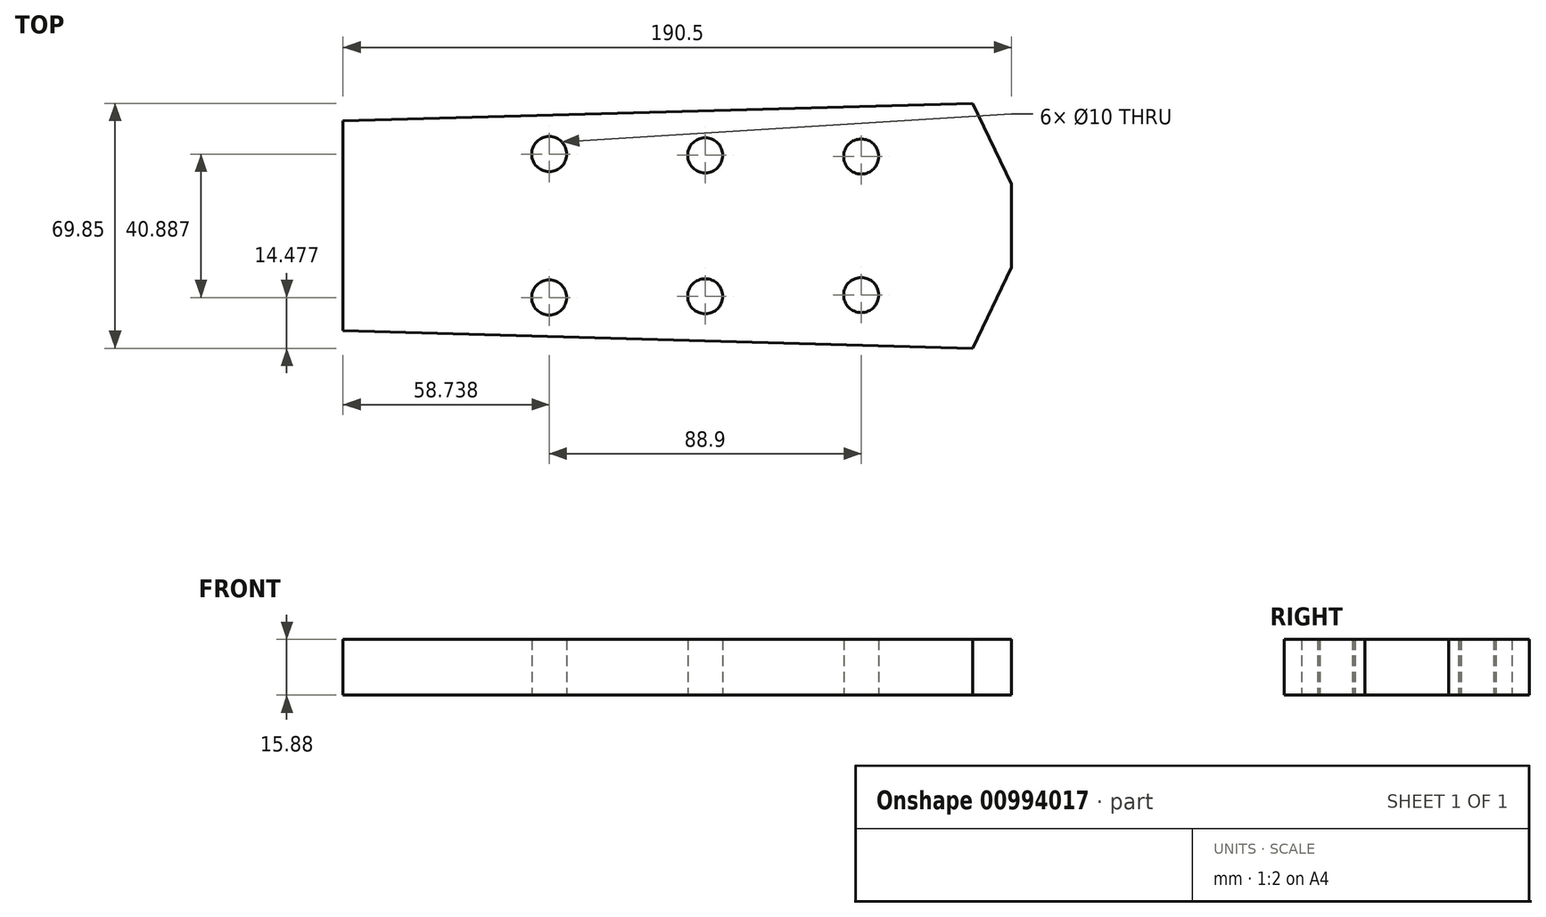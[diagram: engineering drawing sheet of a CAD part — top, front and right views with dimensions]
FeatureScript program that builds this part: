
annotation { "Feature Type Name" : "Feature", "Feature Type Description" : "" }
export const myFeature = defineFeature(function(context is Context, id is Id, definition is map)
    precondition{}
    {
        {
            var Q0;
            Q0=qCreatedBy(makeId("Top.planeOp"),FACE);
            var sketch = newSketch(context, id + "F0", { "sketchPlane" : qUnion([Q0])});
            skLineSegment(sketch, "E0", {"start": v(0, 0) * mm, "end": v(-179.39, 0) * mm, "construction": true});
            skLineSegment(sketch, "E1", {"start": v(0, 0) * mm, "end": v(0, 11.9) * mm});
            skLineSegment(sketch, "E2.bottom", {"start": v(-179.39, 0) * mm, "end": v(-11.11, 0) * mm, "construction": true});
            skLineSegment(sketch, "E2.left", {"start": v(-179.39, 0) * mm, "end": v(-179.39, 30.23) * mm, "construction": true});
            skPoint(sketch, "E3", {"position": v(-179.39, 30.23) * mm});
            skLineSegment(sketch, "E4", {"start": v(-11.11, 34.92) * mm, "end": v(0, 11.9) * mm});
            skLineSegment(sketch, "E5", {"start": v(-131.76, 31.56) * mm, "end": v(-131.76, 20.44) * mm, "construction": true});
            skLineSegment(sketch, "E6", {"start": v(-87.31, 20.1) * mm, "end": v(-87.31, 32.8) * mm, "construction": true});
            skLineSegment(sketch, "E7", {"start": v(-42.86, 19.75) * mm, "end": v(-42.86, 34.04) * mm, "construction": true});
            skCircle(sketch, "E8", {"center": v(-131.76, 20.44) * mm, "radius": 5 * mm});
            skCircle(sketch, "E9", {"center": v(-87.31, 20.1) * mm, "radius": 5 * mm});
            skCircle(sketch, "E10", {"center": v(-42.86, 19.75) * mm, "radius": 5 * mm});
            skLineSegment(sketch, "E11", {"start": v(-190.5, 29.92) * mm, "end": v(-190.5, 0) * mm});
            skLineSegment(sketch, "E12", {"start": v(-11.11, 0) * mm, "end": v(-11.11, 34.93) * mm, "construction": true});
            skLineSegment(sketch, "E13", {"start": v(-11.11, 34.92) * mm, "end": v(-190.5, 29.92) * mm});
            skLineSegment(sketch, "E14", {"start": v(-179.39, 0) * mm, "end": v(-190.5, 0) * mm, "construction": true});
            skLineSegment(sketch, "E15.MirrorCS", {"start": v(-190.5, -29.92) * mm, "end": v(-190.5, 0) * mm});
            skLineSegment(sketch, "E16.MirrorCS", {"start": v(-11.11, -34.93) * mm, "end": v(-190.5, -29.92) * mm});
            skLineSegment(sketch, "E17.MirrorCS", {"start": v(-11.11, -34.93) * mm, "end": v(0, -11.9) * mm});
            skLineSegment(sketch, "E18.MirrorCS", {"start": v(0, 0) * mm, "end": v(0, -11.9) * mm});
            skCircle(sketch, "E19.MirrorC", {"center": v(-42.86, -19.75) * mm, "radius": 5 * mm});
            skCircle(sketch, "E20.MirrorC", {"center": v(-87.31, -20.1) * mm, "radius": 5 * mm});
            skCircle(sketch, "E21.MirrorC", {"center": v(-131.76, -20.44) * mm, "radius": 5 * mm});
            skPoint(sketch, "E22", {"position": v(-179.39, -30.23) * mm});
            skSolve(sketch);
        }
        {
            var Q0;
            Q0=makeQuery(id+"F0.imprint","IMPRINT",FACE,{"disambiguationData":[TD([[makeQuery(id+"F0.imprint","IMPRINT",EDGE,{"derivedFrom":sQuery(id+"F0.wireOp",EDGE,"E1")}),1.0]])]});
            extrude(context, id + "F1", {"entities" : qUnion([Q0]), "depth" : 15.88 * mm, "offsetDistance" : 25.4 * mm});
        }
    });
